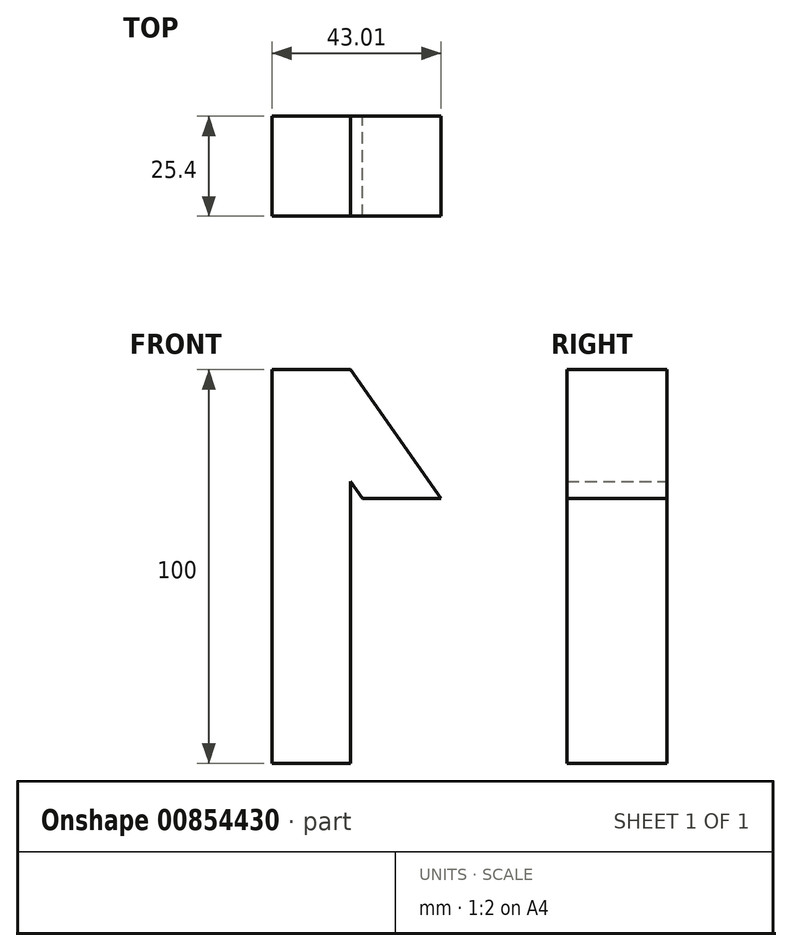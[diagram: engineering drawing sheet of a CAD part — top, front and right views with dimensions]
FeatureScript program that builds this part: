
annotation { "Feature Type Name" : "Feature", "Feature Type Description" : "" }
export const myFeature = defineFeature(function(context is Context, id is Id, definition is map)
    precondition{}
    {
        {
            var Q0;
            Q0=qCreatedBy(makeId("Front.planeOp"),FACE);
            var sketch = newSketch(context, id + "F0", { "sketchPlane" : qUnion([Q0])});
            skLineSegment(sketch, "E0.bottom", {"start": v(-10, 50) * mm, "end": v(10, 50) * mm});
            skLineSegment(sketch, "E0.top", {"start": v(-10, -50) * mm, "end": v(10, -50) * mm});
            skLineSegment(sketch, "E0.left", {"start": v(-10, 50) * mm, "end": v(-10, -50) * mm});
            skLineSegment(sketch, "E0.right", {"start": v(10, 50) * mm, "end": v(10, -50) * mm});
            skPoint(sketch, "E0.middle", {"position": v(0, 0) * mm});
            skLineSegment(sketch, "E1", {"start": v(-10, 50) * mm, "end": v(13.01, 17.28) * mm});
            skLineSegment(sketch, "E2", {"start": v(13.01, 17.28) * mm, "end": v(33.01, 17.28) * mm});
            skLineSegment(sketch, "E3", {"start": v(33.01, 17.28) * mm, "end": v(10, 50) * mm});
            skSolve(sketch);
        }
        {
            var Q0;
            Q0 = qSketchRegion(id + "F0", true);
            extrude(context, id + "F1", {"entities" : qUnion([Q0]), "depth" : 25.4 * mm, "offsetDistance" : 25.4 * mm});
        }
    });
